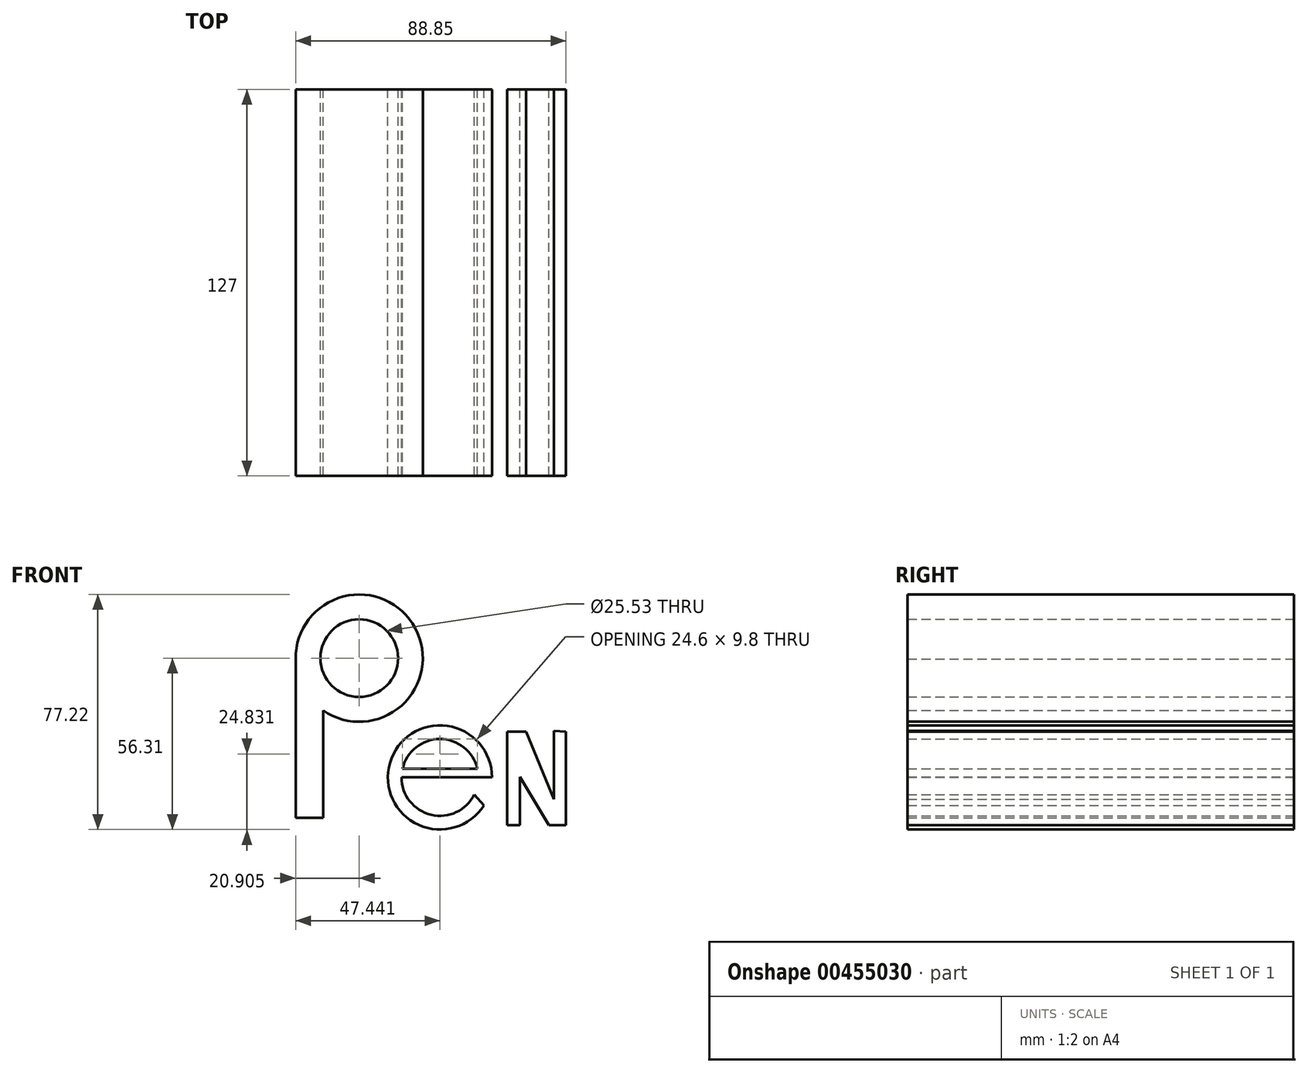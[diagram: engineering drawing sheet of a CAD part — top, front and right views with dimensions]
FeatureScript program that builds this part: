
annotation { "Feature Type Name" : "Feature", "Feature Type Description" : "" }
export const myFeature = defineFeature(function(context is Context, id is Id, definition is map)
    precondition{}
    {
        {
            var Q0;
            Q0=qCreatedBy(makeId("Front.planeOp"),FACE);
            var sketch = newSketch(context, id + "F0", { "sketchPlane" : qUnion([Q0])});
            skLineSegment(sketch, "E0.top", {"start": v(-53.07, -21.3) * mm, "end": v(-44.03, -21.3) * mm});
            skLineSegment(sketch, "E0.left", {"start": v(-53.07, 31.44) * mm, "end": v(-53.07, -21.3) * mm});
            skLineSegment(sketch, "E0.right", {"start": v(-44.03, 13.94) * mm, "end": v(-44.03, -21.3) * mm});
            skArc(sketch, "E1", {"start": v(-44.03, 13.94) * mm, "mid": v(-13.72, 41.01) * mm, "end": v(-53.07, 30.88) * mm});
            skCircle(sketch, "E2", {"center": v(-32.16, 31.16) * mm, "radius": 12.77 * mm});
            skArc(sketch, "E3", {"start": v(6.67, -5.22) * mm, "mid": v(-5.63, 4.58) * mm, "end": v(-17.93, -5.22) * mm});
            skLineSegment(sketch, "E4", {"start": v(-5.63, -8.04) * mm, "end": v(7, -8.04) * mm});
            skLineSegment(sketch, "E5", {"start": v(-5.63, -8.04) * mm, "end": v(-18.25, -8.04) * mm});
            skPoint(sketch, "E6", {"position": v(5.68, -13.65) * mm});
            skArc(sketch, "E7", {"start": v(11.48, -8.04) * mm, "mid": v(-22.06, -3.27) * mm, "end": v(8.82, -17.2) * mm});
            skLineSegment(sketch, "E8", {"start": v(5.68, -13.65) * mm, "end": v(8.82, -17.2) * mm});
            skLineSegment(sketch, "E9", {"start": v(7, -8.04) * mm, "end": v(11.48, -8.04) * mm});
            skLineSegment(sketch, "E10", {"start": v(-17.93, -5.22) * mm, "end": v(6.67, -5.22) * mm});
            skArc(sketch, "E11.trimOffspring", {"start": v(-18.25, -8.04) * mm, "mid": v(-8.5, -20.33) * mm, "end": v(5.68, -13.65) * mm});
            skLineSegment(sketch, "E12", {"start": v(16.48, 7.04) * mm, "end": v(16.48, -23.72) * mm});
            skLineSegment(sketch, "E13", {"start": v(16.48, -23.72) * mm, "end": v(20.7, -23.72) * mm});
            skLineSegment(sketch, "E14", {"start": v(20.7, -23.72) * mm, "end": v(20.7, -7.84) * mm});
            skLineSegment(sketch, "E15", {"start": v(20.7, -7.84) * mm, "end": v(30.15, -23.72) * mm});
            skLineSegment(sketch, "E16", {"start": v(30.15, -23.72) * mm, "end": v(35.78, -23.72) * mm});
            skLineSegment(sketch, "E17", {"start": v(35.78, -23.72) * mm, "end": v(35.78, 7.04) * mm});
            skLineSegment(sketch, "E18", {"start": v(35.78, 7.04) * mm, "end": v(31.76, 7.22) * mm});
            skLineSegment(sketch, "E19", {"start": v(31.76, 7.22) * mm, "end": v(31.76, -15.28) * mm});
            skLineSegment(sketch, "E20", {"start": v(31.76, -15.28) * mm, "end": v(22.72, 7.04) * mm});
            skLineSegment(sketch, "E21", {"start": v(22.72, 7.04) * mm, "end": v(16.48, 7.04) * mm});
            skSolve(sketch);
        }
        {
            var Q0;
            Q0 = qSketchRegion(id + "F0", true);
            extrude(context, id + "F1", {"entities" : qUnion([Q0]), "depth" : 127 * mm});
        }
    });
